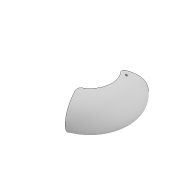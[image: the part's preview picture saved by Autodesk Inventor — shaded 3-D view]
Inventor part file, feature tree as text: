
AUTODESK INVENTOR PART (.ipt)
format: ipt  version: 2022 (Build 260153000, 153)  size: 462,336 bytes
history: native  units: mm
features: sketch x6, extrude x5, thicken_offset x2, plane x2, revolve x1, chamfer x1, fillet x1, projected_geometry x1
ambient origin geometry x8: Origin, YZ Plane, XZ Plane, XY Plane, X Axis, Y Axis, Z Axis, Center Point
bodies: Solid1 (feature_tree)
feature tree (19):
  revolve  "Revolution1"  [1 undecoded]
  thicken_offset  "Thicken1"
  thicken_offset  "Thicken2"
  extrude  "Extrusion1"  Depth=27.925268mm
  extrude  "Extrusion2"  Depth=20.0mm TaperAngle=0.0deg
  extrude  "Extrusion3"  Depth=2.1mm
  plane  "Work Plane2"
  extrude  "Extrusion7"  Depth=18.0mm
  plane  "Work Plane4"
  extrude  "Extrusion9"  Depth=5.0mm TaperAngle=0.0deg
  chamfer  "Chamfer3"  Distance=30.0mm
  fillet  "Fillet1"  Radius=50.0mm
  sketch  "Sketch1"  dims[d2=45.0mm d3=40.0mm]
  sketch  "Sketch2"  dims[d4=2.0mm d5=27.925268mm]
  sketch  "Sketch3"  dims[d6=30.0mm d7=20.0mm d8=0.0mm]
  sketch  "Sketch4"  dims[d9=2.1mm d10=2.1mm]
  projected_geometry  "Projected Loop1"
  sketch  "Sketch8"  dims[d12=4.5mm d14=18.0mm]
  sketch  "Sketch10"  dims[d15=100.0mm d16=0.0mm d18=100.0mm d19=0.0mm d38=30.0mm d39=50.0mm d40=20.0mm d41=0.0mm d46=2.3mm d47=2.0mm d48=2.3mm d49=2.0mm d50=1.7mm d51=3.0mm d52=3.0mm d53=0.0mm d54=23.6mm d55=23.6mm d56=6.981317mm d57=1.0mm d58=2.0mm d59=45.0deg d60=5.0mm]
note: 1 required parameter value undecoded (feature->parameter linkage not recoverable at this tier; creation-order binding heuristic only, values carry confidence <= 0.55)
